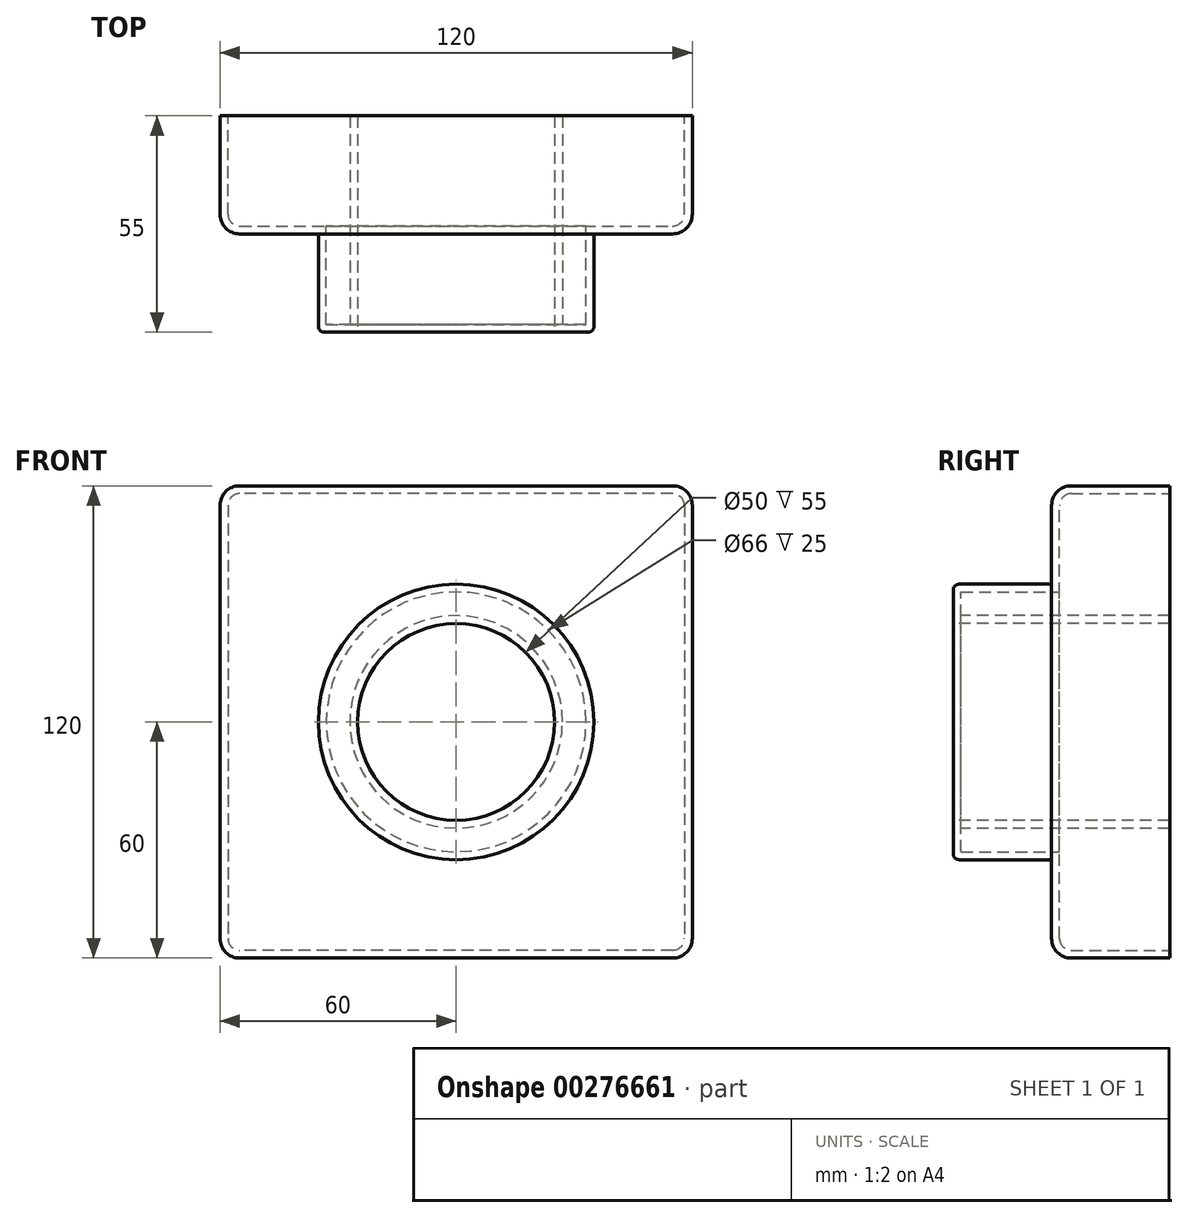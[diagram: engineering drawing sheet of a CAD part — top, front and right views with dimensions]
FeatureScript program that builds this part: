
annotation { "Feature Type Name" : "Feature", "Feature Type Description" : "" }
export const myFeature = defineFeature(function(context is Context, id is Id, definition is map)
    precondition{}
    {
        {
            var Q0;
            Q0=qCreatedBy(makeId("Front.planeOp"),FACE);
            var sketch = newSketch(context, id + "F0", { "sketchPlane" : qUnion([Q0])});
            skLineSegment(sketch, "E0.bottom", {"start": v(60, 60) * mm, "end": v(-60, 60) * mm});
            skLineSegment(sketch, "E0.top", {"start": v(60, -60) * mm, "end": v(-60, -60) * mm});
            skLineSegment(sketch, "E0.left", {"start": v(60, 60) * mm, "end": v(60, -60) * mm});
            skLineSegment(sketch, "E0.right", {"start": v(-60, 60) * mm, "end": v(-60, -60) * mm});
            skPoint(sketch, "E0.middle", {"position": v(0, 0) * mm});
            skSolve(sketch);
        }
        {
            var Q0;
            Q0 = qSketchRegion(id + "F0", true);
            extrude(context, id + "F1", {"entities" : qUnion([Q0]), "depth" : 30 * mm});
        }
        {
            var Q0;
            Q0=makeQuery(id+"F1.opExtrude","CAP_FACE",FACE,{"disambiguationData":[OSD([sQuery(id+"F0.wireOp",EDGE,"E0.bottom"),sQuery(id+"F0.wireOp",EDGE,"E0.top"),sQuery(id+"F0.wireOp",EDGE,"E0.left"),sQuery(id+"F0.wireOp",EDGE,"E0.right")])],"isStart":false});
            var sketch = newSketch(context, id + "F2", { "sketchPlane" : qUnion([Q0])});
            skCircle(sketch, "E1", {"center": v(0, 0) * mm, "radius": 35 * mm});
            skSolve(sketch);
        }
        {
            var Q0;
            Q0=makeQuery(id+"F2.imprint","IMPRINT",FACE,{"disambiguationData":[TD([[makeQuery(id+"F2.imprint","IMPRINT",EDGE,{"derivedFrom":sQuery(id+"F2.wireOp",EDGE,"E1")}),1.0]])]});
            extrude(context, id + "F3", {"entities" : qUnion([Q0]), "operationType" : NewBodyOperationType.ADD, "depth" : 25 * mm});
        }
        {
            var Q0;
            Q0=makeQuery(id+"F3.opExtrude","CAP_FACE",FACE,{"disambiguationData":[OSD([sQuery(id+"F2.wireOp",EDGE,"E1")])],"isStart":false});
            var sketch = newSketch(context, id + "F4", { "sketchPlane" : qUnion([Q0])});
            skCircle(sketch, "E2", {"center": v(0, 0) * mm, "radius": 25 * mm});
            skSolve(sketch);
        }
        {
            var Q0;
            Q0 = qSketchRegion(id + "F4", true);
            extrude(context, id + "F5", {"entities" : qUnion([Q0]), "operationType" : NewBodyOperationType.REMOVE, "endBound" : BoundingType.THROUGH_ALL, "oppositeDirection" : true, "depth" : 25 * mm});
        }
        {
            var Q0;
            Q0=makeQuery(id+"F3.opExtrude","CAP_EDGE",EDGE,{"disambiguationData":[OSD([sQuery(id+"F2.wireOp",EDGE,"E1")])],"isStart":true});
            var Q1;
            Q1=makeQuery(id+"F1.opExtrude","CAP_EDGE",EDGE,{"disambiguationData":[OSD([sQuery(id+"F0.wireOp",EDGE,"E0.bottom")])],"isStart":false});
            var Q2;
            Q2=makeQuery(id+"F1.opExtrude","CAP_EDGE",EDGE,{"disambiguationData":[OSD([sQuery(id+"F0.wireOp",EDGE,"E0.left")])],"isStart":false});
            var Q3;
            Q3=makeQuery(id+"F1.opExtrude","SWEPT_EDGE",EDGE,{"disambiguationData":[OSD([sQuery(id+"F0.wireOp",EDGE,"E0.bottom"),sQuery(id+"F0.wireOp",EDGE,"E0.left")])]});
            var Q4;
            Q4=makeQuery(id+"F1.opExtrude","SWEPT_EDGE",EDGE,{"disambiguationData":[OSD([sQuery(id+"F0.wireOp",EDGE,"E0.top"),sQuery(id+"F0.wireOp",EDGE,"E0.left")])]});
            var Q5;
            Q5=makeQuery(id+"F1.opExtrude","CAP_EDGE",EDGE,{"disambiguationData":[OSD([sQuery(id+"F0.wireOp",EDGE,"E0.top")])],"isStart":false});
            var Q6;
            Q6=makeQuery(id+"F1.opExtrude","SWEPT_EDGE",EDGE,{"disambiguationData":[OSD([sQuery(id+"F0.wireOp",EDGE,"E0.top"),sQuery(id+"F0.wireOp",EDGE,"E0.right")])]});
            var Q7;
            Q7=makeQuery(id+"F1.opExtrude","CAP_EDGE",EDGE,{"disambiguationData":[OSD([sQuery(id+"F0.wireOp",EDGE,"E0.right")])],"isStart":false});
            var Q8;
            Q8=makeQuery(id+"F1.opExtrude","SWEPT_EDGE",EDGE,{"disambiguationData":[OSD([sQuery(id+"F0.wireOp",EDGE,"E0.bottom"),sQuery(id+"F0.wireOp",EDGE,"E0.right")])]});
            fillet(context, id + "F6", {"entities" : qUnion([Q0, Q1, Q2, Q3, Q4, Q5, Q6, Q7, Q8]), "radius" : 5 * mm, "tangentPropagation" : true, "allowEdgeOverflow" : false});
        }
        {
            var Q0;
            Q0=makeQuery(id+"F3.opExtrude","CAP_EDGE",EDGE,{"disambiguationData":[OSD([sQuery(id+"F2.wireOp",EDGE,"E1")])],"isStart":false});
            fillet(context, id + "F7", {"entities" : qUnion([Q0]), "radius" : 1.5 * mm, "tangentPropagation" : true, "allowEdgeOverflow" : false});
        }
        {
            var Q0;
            Q0=makeQuery(id+"F1.opExtrude","CAP_FACE",FACE,{"disambiguationData":[OSD([sQuery(id+"F0.wireOp",EDGE,"E0.bottom"),sQuery(id+"F0.wireOp",EDGE,"E0.top"),sQuery(id+"F0.wireOp",EDGE,"E0.left"),sQuery(id+"F0.wireOp",EDGE,"E0.right")])],"isStart":true});
            shell(context, id + "F8", {"entities" : qUnion([Q0]), "thickness" : 2 * mm});
        }
    });
